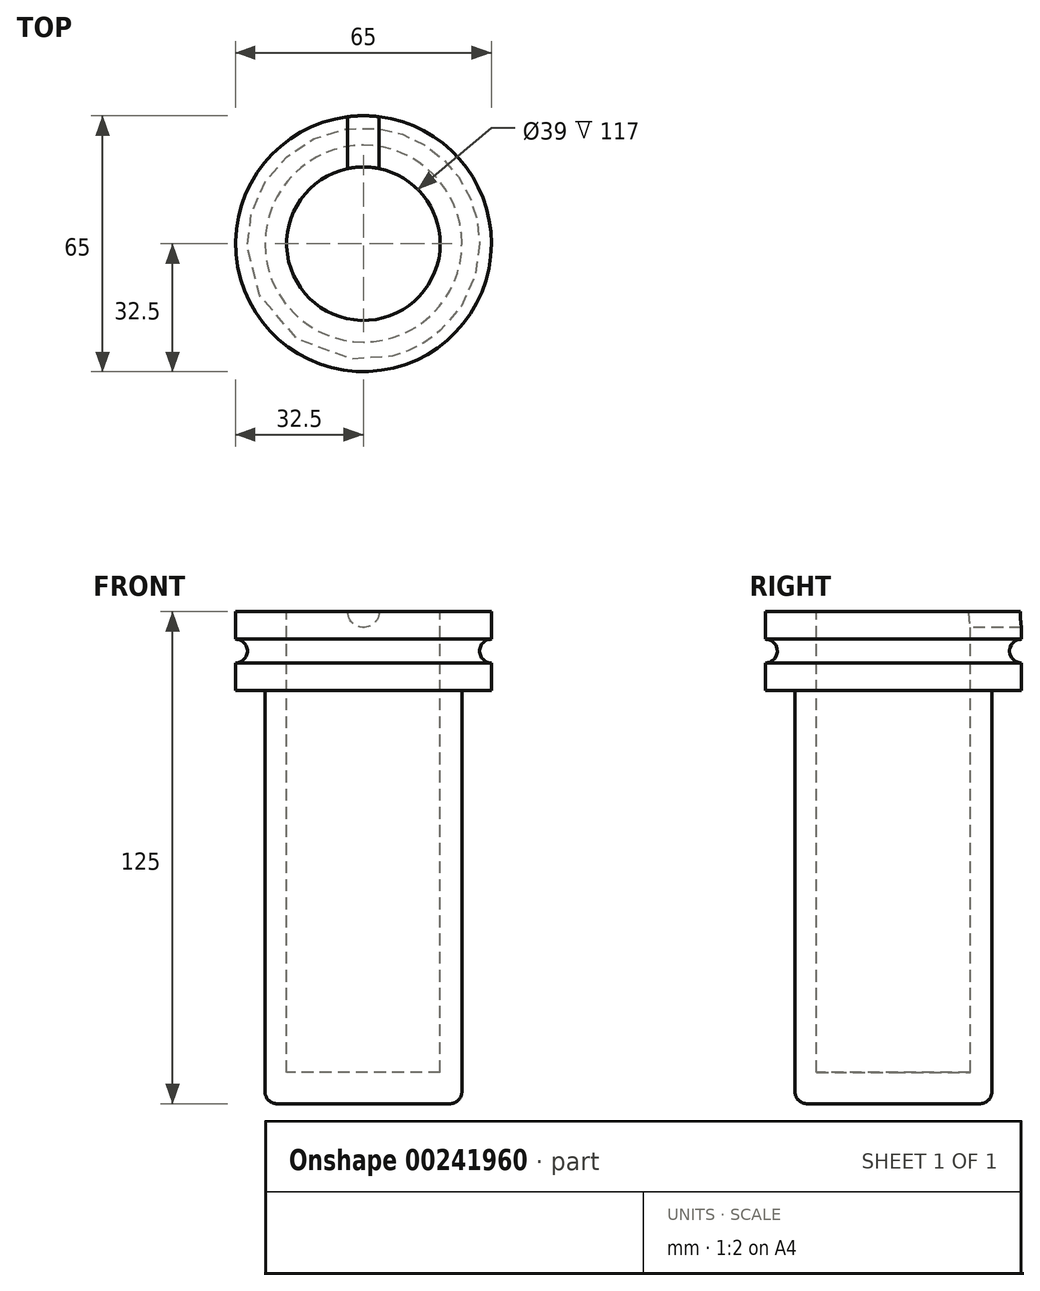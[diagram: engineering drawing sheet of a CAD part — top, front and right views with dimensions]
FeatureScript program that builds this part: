
annotation { "Feature Type Name" : "Feature", "Feature Type Description" : "" }
export const myFeature = defineFeature(function(context is Context, id is Id, definition is map)
    precondition{}
    {
        {
            var Q0;
            Q0=qCreatedBy(makeId("Front.planeOp"),FACE);
            var sketch = newSketch(context, id + "F0", { "sketchPlane" : qUnion([Q0])});
            skLineSegment(sketch, "E0", {"start": v(0, 0) * mm, "end": v(-22, 0) * mm});
            skLineSegment(sketch, "E1", {"start": v(-25, 3) * mm, "end": v(-25, 105) * mm});
            skLineSegment(sketch, "E2", {"start": v(-25, 105) * mm, "end": v(-32.5, 105) * mm});
            skLineSegment(sketch, "E3", {"start": v(-32.5, 105) * mm, "end": v(-32.5, 112) * mm});
            skLineSegment(sketch, "E4", {"start": v(-32.5, 125) * mm, "end": v(-19.5, 125) * mm});
            skLineSegment(sketch, "E5", {"start": v(-19.5, 125) * mm, "end": v(-19.5, 8) * mm});
            skLineSegment(sketch, "E6", {"start": v(-19.5, 8) * mm, "end": v(0, 8) * mm});
            skLineSegment(sketch, "E7", {"start": v(0, 8) * mm, "end": v(0, 0) * mm});
            skArc(sketch, "E8", {"start": v(-32.5, 112) * mm, "mid": v(-29.5, 115) * mm, "end": v(-32.5, 118) * mm});
            skLineSegment(sketch, "E9.trimOffspring", {"start": v(-32.5, 118) * mm, "end": v(-32.5, 125) * mm});
            skPoint(sketch, "E10.visualSharp", {"position": v(-25, 0) * mm});
            skArc(sketch, "E10.filletArc", {"start": v(-25, 3) * mm, "mid": v(-24.12, 0.88) * mm, "end": v(-22, 0) * mm});
            skSolve(sketch);
        }
        {
            var Q0;
            Q0 = qSketchRegion(id + "F0", true);
            var Q1;
            Q1=sQuery(id+"F0.wireOp",EDGE,"E7");
            revolve(context, id + "F1", {"entities" : qUnion([Q0]), "axis" : qUnion([Q1]), "revolveType" : RevolveType.FULL});
        }
        {
            var Q0;
            Q0=qCreatedBy(makeId("Front.planeOp"),FACE);
            var sketch = newSketch(context, id + "F2", { "sketchPlane" : qUnion([Q0])});
            skLineSegment(sketch, "E11.0", {"start": v(-32.5, 125) * mm, "end": v(32.5, 125) * mm, "construction": true});
            skCircle(sketch, "E12", {"center": v(0, 125) * mm, "radius": 4 * mm});
            skSolve(sketch);
        }
        {
            var Q0;
            Q0=makeQuery(id+"F2.imprint","IMPRINT",FACE,{"disambiguationData":[TD([[makeQuery(id+"F2.imprint","IMPRINT",EDGE,{"derivedFrom":sQuery(id+"F2.wireOp",EDGE,"E12")}),1.0]])]});
            var Q1;
            Q1=sQuery(id+"F2.wireOp",EDGE,"E12");
            extrude(context, id + "F3", {"entities" : qUnion([Q0]), "operationType" : NewBodyOperationType.REMOVE, "surfaceEntities" : qUnion([Q1]), "oppositeDirection" : true, "depth" : 50 * mm});
        }
    });
